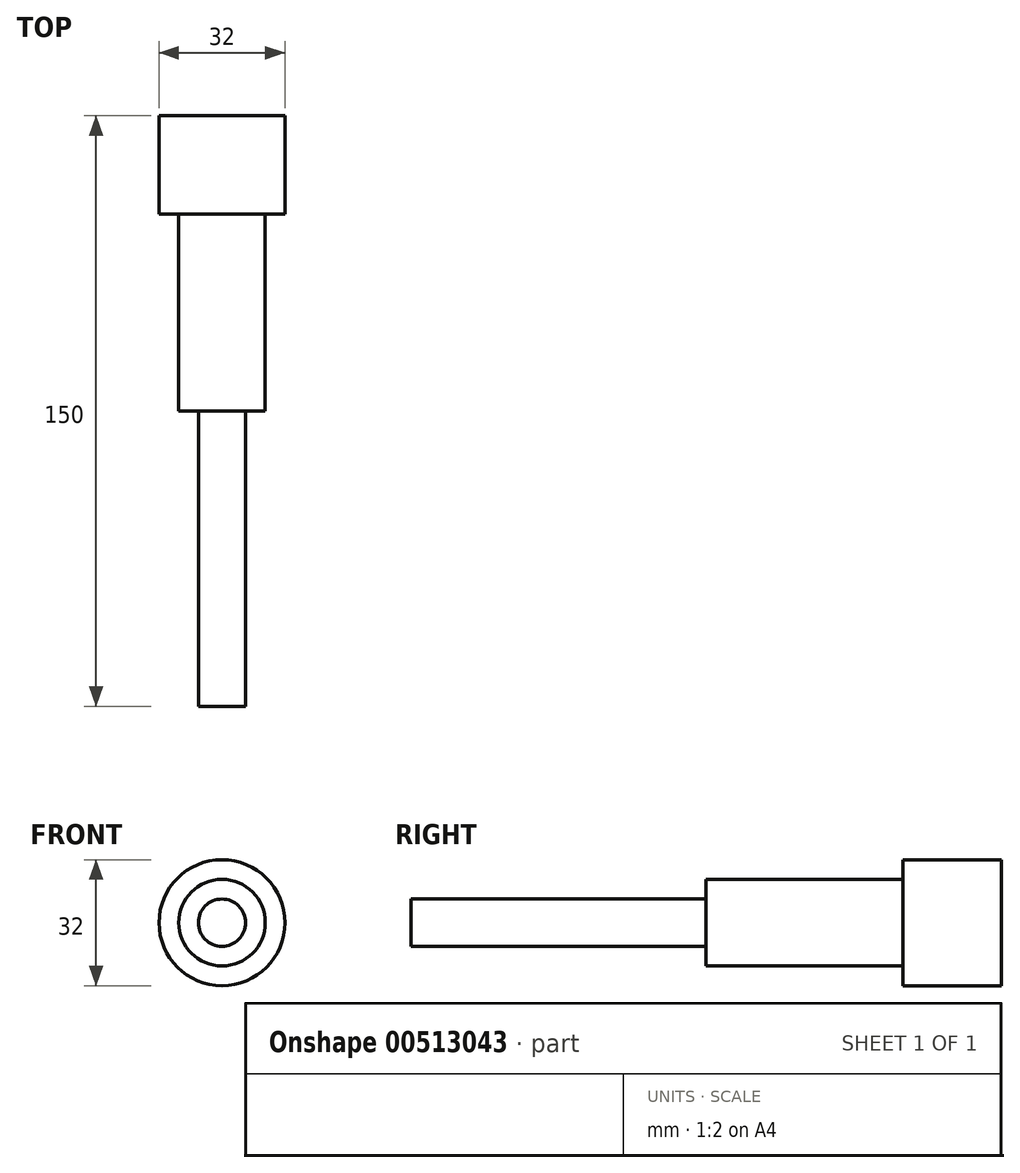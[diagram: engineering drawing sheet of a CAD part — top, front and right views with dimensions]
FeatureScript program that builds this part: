
annotation { "Feature Type Name" : "Feature", "Feature Type Description" : "" }
export const myFeature = defineFeature(function(context is Context, id is Id, definition is map)
    precondition{}
    {
        {
            var Q0;
            Q0=qCreatedBy(makeId("Front.planeOp"),FACE);
            var sketch = newSketch(context, id + "F0", { "sketchPlane" : qUnion([Q0])});
            skCircle(sketch, "E0", {"center": v(0, 0) * mm, "radius": 16 * mm});
            skSolve(sketch);
        }
        {
            var Q0;
            Q0=makeQuery(id+"F0.imprint","IMPRINT",FACE,{"disambiguationData":[TD([[makeQuery(id+"F0.imprint","IMPRINT",EDGE,{"derivedFrom":sQuery(id+"F0.wireOp",EDGE,"E0")}),1.0]])]});
            extrude(context, id + "F1", {"entities" : qUnion([Q0]), "depth" : 25 * mm, "offsetDistance" : 25 * mm});
        }
        {
            var Q0;
            Q0=makeQuery(id+"F1.opExtrude","CAP_FACE",FACE,{"disambiguationData":[OSD([sQuery(id+"F0.wireOp",EDGE,"E0")])],"isStart":false});
            var sketch = newSketch(context, id + "F2", { "sketchPlane" : qUnion([Q0])});
            skCircle(sketch, "E1", {"center": v(0, 0) * mm, "radius": 11 * mm});
            skSolve(sketch);
        }
        {
            var Q0;
            Q0 = qSketchRegion(id + "F2", true);
            extrude(context, id + "F3", {"entities" : qUnion([Q0]), "operationType" : NewBodyOperationType.ADD, "depth" : 50 * mm, "offsetDistance" : 25 * mm});
        }
        {
            var Q0;
            Q0=makeQuery(id+"F3.opExtrude","CAP_FACE",FACE,{"disambiguationData":[OSD([sQuery(id+"F2.wireOp",EDGE,"E1")])],"isStart":false});
            var sketch = newSketch(context, id + "F4", { "sketchPlane" : qUnion([Q0])});
            skCircle(sketch, "E2", {"center": v(0, 0) * mm, "radius": 6 * mm});
            skSolve(sketch);
        }
        {
            var Q0;
            Q0=makeQuery(id+"F4.imprint","IMPRINT",FACE,{"disambiguationData":[TD([[makeQuery(id+"F4.imprint","IMPRINT",EDGE,{"derivedFrom":sQuery(id+"F4.wireOp",EDGE,"E2")}),1.0]])]});
            var Q1;
            Q1=sQuery(id+"F4.wireOp",EDGE,"E2");
            extrude(context, id + "F5", {"entities" : qUnion([Q0]), "operationType" : NewBodyOperationType.ADD, "surfaceEntities" : qUnion([Q1]), "depth" : 75 * mm, "offsetDistance" : 25 * mm});
        }
    });
